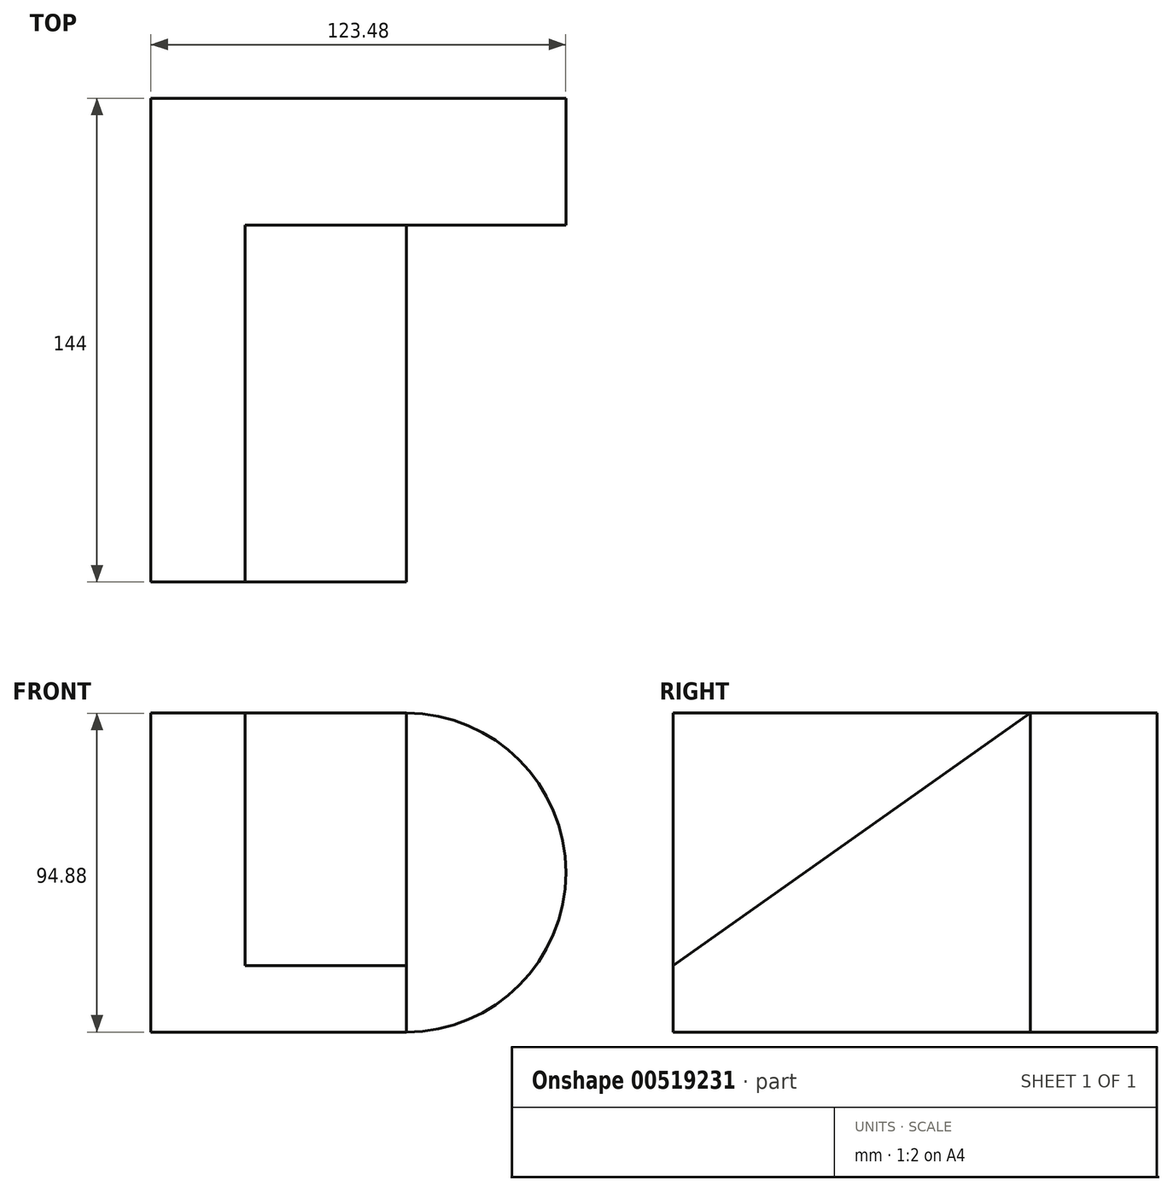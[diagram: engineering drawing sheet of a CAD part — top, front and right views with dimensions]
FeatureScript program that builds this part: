
annotation { "Feature Type Name" : "Feature", "Feature Type Description" : "" }
export const myFeature = defineFeature(function(context is Context, id is Id, definition is map)
    precondition{}
    {
        {
            var Q0;
            Q0=qCreatedBy(makeId("Front.planeOp"),FACE);
            var sketch = newSketch(context, id + "F0", { "sketchPlane" : qUnion([Q0])});
            skArc(sketch, "E0", {"start": v(0, -47.44) * mm, "mid": v(47.44, 0) * mm, "end": v(0, 47.44) * mm});
            skLineSegment(sketch, "E1.bottom", {"start": v(0, -47.44) * mm, "end": v(-76.04, -47.44) * mm});
            skLineSegment(sketch, "E1.top", {"start": v(0, 47.44) * mm, "end": v(-76.04, 47.44) * mm});
            skLineSegment(sketch, "E1.right", {"start": v(-76.04, -47.44) * mm, "end": v(-76.04, 47.44) * mm});
            skSolve(sketch);
        }
        {
            var Q0;
            Q0=makeQuery(id+"F0.imprint","IMPRINT",FACE,{"disambiguationData":[TD([[makeQuery(id+"F0.imprint","IMPRINT",EDGE,{"derivedFrom":sQuery(id+"F0.wireOp",EDGE,"E0")}),1.0]])]});
            extrude(context, id + "F1", {"entities" : qUnion([Q0]), "endBound" : BoundingType.SYMMETRIC, "depth" : 144 * mm, "offsetDistance" : 25 * mm});
        }
        {
            var Q0;
            Q0=makeQuery(id+"F1.opExtrude","CAP_EDGE",EDGE,{"disambiguationData":[OSD([sQuery(id+"F0.wireOp",EDGE,"E0")])],"isStart":true});
            cPoint(context, id + "F2", {"entities" : qUnion([Q0]), "parameter" : 0.5});
        }
        {
            var Q0;
            Q0=qCreatedBy(makeId("Right.planeOp"),FACE);
            var Q1;
            Q1 = qCreatedBy(id + "F2" ,VERTEX);
            cPlane(context, id + "F3", {"entities" : qUnion([Q0, Q1]), "cplaneType" : CPlaneType.PLANE_POINT, "offset" : 25 * mm, "width" : 150 * mm, "height" : 150 * mm});
        }
        {
            var Q0;
            Q0=qCreatedBy(id+"F3.planeOp",FACE);
            var sketch = newSketch(context, id + "F4", { "sketchPlane" : qUnion([Q0])});
            skLineSegment(sketch, "E2.0", {"start": v(-72, -47.44) * mm, "end": v(-72, 47.44) * mm});
            skLineSegment(sketch, "E3.0", {"start": v(-72, 47.44) * mm, "end": v(34.21, 47.44) * mm});
            skLineSegment(sketch, "E4.0", {"start": v(-72, -47.44) * mm, "end": v(34.21, -47.44) * mm});
            skLineSegment(sketch, "E5", {"start": v(34.21, 47.44) * mm, "end": v(34.21, -47.44) * mm});
            skSolve(sketch);
        }
        {
            var Q0;
            Q0=makeQuery(id+"F4.imprint","IMPRINT",FACE,{"disambiguationData":[TD([[makeQuery(id+"F4.imprint","IMPRINT",EDGE,{"derivedFrom":sQuery(id+"F4.wireOp",EDGE,"E2.0")}),-1.0]])]});
            var Q1;
            Q1=makeQuery(id+"F1.opExtrude","CAP_VERTEX",VERTEX,{"disambiguationData":[OSD([sQuery(id+"F0.wireOp",EDGE,"E0"),sQuery(id+"F0.wireOp",EDGE,"E1.top")])],"isStart":false});
            extrude(context, id + "F5", {"entities" : qUnion([Q0]), "operationType" : NewBodyOperationType.REMOVE, "endBound" : BoundingType.UP_TO_VERTEX, "oppositeDirection" : true, "depth" : 39 * mm, "endBoundEntityVertex" : qUnion([Q1]), "offsetDistance" : 25 * mm});
        }
        {
            var Q0;
            Q0=makeQuery(id+"F5.boolean.opBoolean","COPY",FACE,{"derivedFrom":makeQuery(id+"F5.opExtrude","CAP_FACE",FACE,{"disambiguationData":[OSD([sQuery(id+"F4.wireOp",EDGE,"E2.0"),sQuery(id+"F4.wireOp",EDGE,"E3.0"),sQuery(id+"F4.wireOp",EDGE,"E4.0"),sQuery(id+"F4.wireOp",EDGE,"E5")])],"isStart":false})});
            var sketch = newSketch(context, id + "F6", { "sketchPlane" : qUnion([Q0])});
            skLineSegment(sketch, "E6", {"start": v(34.21, 47.44) * mm, "end": v(-72, -27.69) * mm});
            skLineSegment(sketch, "E7", {"start": v(-72, -27.69) * mm, "end": v(-72, 47.44) * mm});
            skLineSegment(sketch, "E8", {"start": v(-72, 47.44) * mm, "end": v(34.21, 47.44) * mm});
            skSolve(sketch);
        }
        {
            var Q0;
            Q0=makeQuery(id+"F6.imprint","IMPRINT",FACE,{"disambiguationData":[TD([[makeQuery(id+"F6.imprint","IMPRINT",EDGE,{"derivedFrom":sQuery(id+"F6.wireOp",EDGE,"E6")}),-1.0]])]});
            extrude(context, id + "F7", {"entities" : qUnion([Q0]), "operationType" : NewBodyOperationType.REMOVE, "oppositeDirection" : true, "depth" : 48 * mm, "offsetDistance" : 25 * mm});
        }
    });
